# Revit family: 712-3810-001-DN40-1200
name_source: partatom
category: Pipe Accessories
units: mm (PartAtom-declared; Revit-internal decimal feet)

## family parameters
Always vertical = Yes
Cut with Voids When Loaded = No
Part Type = Valve - Breaks Into
Round Connector Dimension = Use Diameter
Shared = No
Work Plane-Based = No

## types (27) — shared parameters
Body_wallthickness = 10 mm  [stored 0.0328084 ft]
DN040_PN10/16 = 712-0040-38-101
DN050_PN10/16 = 712-0050-38-101
DN060/065_PN10/16 = 712-0070-38-101
DN060_ PN10/16 = 712-0060-38-101
DN060_PN10/16 = 712-0060-38-103
DN065_PN10/16 = 712-0065-38-101
DN080_PN10/16 = 712-0080-38-101
DN100_PN10/16 = 712-0100-38-101
DN1200_PN10 = 712-1200-38-100
DN125_PN10/16 = 712-0125-38-101
DN150_PN10/16 = 712-0150-38-101
DN200_PN10 = 712-0200-38-100
DN200_PN16 = 712-0200-38-101
DN250_PN10 = 712-0250-38-100
DN250_PN16 = 712-0250-38-101
DN300_PN10 = 712-0250-38-101
DN300_PN16 = 712-0300-38-101
DN350_PN10 = 712-0350-38-100
DN350_PN16 = 712-0350-38-101
DN400_PN10 = 712-0400-38-100
DN400_PN16 = 712-0400-38-101
DN450_PN10 = 712-0450-38-100
DN450_PN16 = 712-0450-38-101
DN500_PN10 = 712-0500-38-100
DN500_PN16 = 712-0500-38-101
DN600_PN10 = 712-0600-38-100
DN600_PN16 = 712-0600-38-101
Description_ = AVK BLIND FLANGE
Search_Table = 712-3810-001-DN40-1200
URL product pages = https://www.avkvalves.com

## per-type parameters (varying)
| type | D | ID(Radius) | L | Nominal Diameter (DN) | RF_Thick | Rf_Dia | Rib |
| DN0300_PN16 | 228 mm | 150 mm | 25 mm  [stored 0.082021 ft] | 300 mm | 4 mm  [stored 0.0131234 ft] | 185 mm | 75 mm |
| DN0350_PN10 | 253 mm | 175 mm | 25 mm  [stored 0.082021 ft] | 350 mm | 4 mm  [stored 0.0131234 ft] | 215 mm | 88 mm |
| DN0350_PN16 | 260 mm | 175 mm | 27 mm  [stored 0.0885827 ft] | 350 mm | 4 mm  [stored 0.0131234 ft] | 215 mm | 88 mm |
| DN0400_PN10 | 283 mm | 200 mm | 25 mm  [stored 0.082021 ft] | 400 mm | 4 mm  [stored 0.0131234 ft] | 240 mm | 100 mm  [stored 0.328084 ft] |
| DN0400_PN16 | 290 mm | 200 mm | 28 mm  [stored 0.0918635 ft] | 400 mm | 4 mm  [stored 0.0131234 ft] | 240 mm | 100 mm  [stored 0.328084 ft] |
| DN0450_PN10 | 308 mm | 225 mm | 26 mm | 450 mm | 4 mm  [stored 0.0131234 ft] | 265 mm | 113 mm |
| DN0450_PN16 | 320 mm | 225 mm | 30 mm  [stored 0.0984252 ft] | 450 mm | 4 mm  [stored 0.0131234 ft] | 274 mm | 113 mm |
| DN0500_PN10 | 335 mm | 250 mm | 27 mm  [stored 0.0885827 ft] | 500 mm | 4 mm  [stored 0.0131234 ft] | 291 mm | 125 mm |
| DN0500_PN16 | 358 mm | 250 mm | 32 mm  [stored 0.104987 ft] | 500 mm | 4 mm  [stored 0.0131234 ft] | 305 mm | 125 mm |
| DN0600_PN10 | 390 mm | 300 mm | 30 mm  [stored 0.0984252 ft] | 600 mm | 5 mm  [stored 0.0164042 ft] | 341 mm | 150 mm |
| DN0600_PN16 | 420 mm | 300 mm | 36 mm  [stored 0.11811 ft] | 600 mm | 5 mm  [stored 0.0164042 ft] | 360 mm | 150 mm |
| DN1200_PN10 | 728 mm | 600 mm | 45 mm  [stored 0.147638 ft] | 1200 mm | 5 mm  [stored 0.0164042 ft] | 664 mm | 300 mm |
| DN0300_PN10 | 228 mm | 150 mm | 25 mm  [stored 0.082021 ft] | 300 mm | 4 mm  [stored 0.0131234 ft] | 185 mm | 75 mm |
| DN0250_PN10 | 200 mm | 125 mm | 22 mm  [stored 0.0721785 ft] | 250 mm | 4 mm  [stored 0.0131234 ft] | 160 mm | 63 mm  [stored 0.206693 ft] |
| DN0250_PN16 | 200 mm | 125 mm | 22 mm  [stored 0.0721785 ft] | 250 mm | 4 mm  [stored 0.0131234 ft] | 160 mm | 63 mm  [stored 0.206693 ft] |
| DN0200_PN10 | 170 mm | 100 mm  [stored 0.328084 ft] | 20 mm  [stored 0.0656168 ft] | 200 mm | 4 mm  [stored 0.0131234 ft] | 133 mm | 50 mm  [stored 0.164042 ft] |
| DN0200_PN16 | 170 mm | 100 mm  [stored 0.328084 ft] | 20 mm  [stored 0.0656168 ft] | 200 mm | 4 mm  [stored 0.0131234 ft] | 133 mm | 50 mm  [stored 0.164042 ft] |
| DN0150_PN10/16 | 143 mm | 75 mm | 19 mm  [stored 0.062336 ft] | 150 mm | 4 mm  [stored 0.0131234 ft] | 106 mm | 38 mm |
| DN0125_PN10/16 | 125 mm | 63 mm  [stored 0.206693 ft] | 19 mm  [stored 0.062336 ft] | 125 mm | 3 mm  [stored 0.00984252 ft] | 92 mm  [stored 0.301837 ft] | 31 mm  [stored 0.101706 ft] |
| DN0100_PN10/16 | 110 mm  [stored 0.360892 ft] | 50 mm  [stored 0.164042 ft] | 19 mm  [stored 0.062336 ft] | 100 mm  [stored 0.328084 ft] | 3 mm  [stored 0.00984252 ft] | 78 mm  [stored 0.255906 ft] | 25 mm  [stored 0.082021 ft] |
| DN0080_PN10/16 | 100 mm  [stored 0.328084 ft] | 40 mm  [stored 0.131234 ft] | 19 mm  [stored 0.062336 ft] | 80 mm  [stored 0.262467 ft] | 3 mm  [stored 0.00984252 ft] | 66 mm  [stored 0.216535 ft] | 20 mm  [stored 0.0656168 ft] |
| DN0060/0065_PN10/16 | 93 mm  [stored 0.305118 ft] | 33 mm | 19 mm  [stored 0.062336 ft] | 65 mm  [stored 0.213255 ft] | 3 mm  [stored 0.00984252 ft] | 59 mm | 16 mm |
| DN0065_PN10/16 | 93 mm  [stored 0.305118 ft] | 33 mm | 19 mm  [stored 0.062336 ft] | 65 mm  [stored 0.213255 ft] | 3 mm  [stored 0.00984252 ft] | 59 mm | 16 mm |
| DN0060_PN10/16 | 88 mm | 30 mm  [stored 0.0984252 ft] | 19 mm  [stored 0.062336 ft] | 60 mm  [stored 0.19685 ft] | 3 mm  [stored 0.00984252 ft] | 54 mm  [stored 0.177165 ft] | 15 mm  [stored 0.0492126 ft] |
| DN0060_ PN10/16 | 88 mm | 30 mm  [stored 0.0984252 ft] | 19 mm  [stored 0.062336 ft] | 60 mm  [stored 0.19685 ft] | 3 mm  [stored 0.00984252 ft] | 54 mm  [stored 0.177165 ft] | 15 mm  [stored 0.0492126 ft] |
| DN0050_PN10/16 | 83 mm | 25 mm  [stored 0.082021 ft] | 19 mm  [stored 0.062336 ft] | 50 mm  [stored 0.164042 ft] | 3 mm  [stored 0.00984252 ft] | 50 mm  [stored 0.164042 ft] | 13 mm |
| DN0040_PN10/16 | 75 mm | 20 mm  [stored 0.0656168 ft] | 19 mm  [stored 0.062336 ft] | 40 mm  [stored 0.131234 ft] | 3 mm  [stored 0.00984252 ft] | 42 mm  [stored 0.137795 ft] | 10 mm  [stored 0.0328084 ft] |

note: [stored X ft] marks values corroborated as IEEE doubles in the binary element streams (Revit-internal decimal feet)

## geometry (parser evidence)
native form markers: Sweep x15
no freeform markers — native parametric forms only
